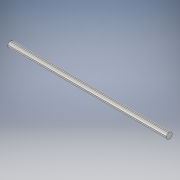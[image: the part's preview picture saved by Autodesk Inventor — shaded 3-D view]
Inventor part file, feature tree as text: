
AUTODESK INVENTOR PART (.ipt)
format: ipt  version: 2018 (Build 220112000, 112)  size: 107,008 bytes
history: native  units: in
note: dims shown in document units (in); Inventor stores cm internally (conversion verified against a paired STEP export)
features: extrude x1, fillet x1, plane x1, sketch x1
ambient origin geometry x8: Origin, YZ Plane, XZ Plane, XY Plane, X Axis, Y Axis, Z Axis, Center Point
bodies: Solid1 (feature_tree)
feature tree (4):
  extrude  "Extrusion1"  Depth=0.1181in
  fillet  "Fillet1"  Radius=3.3465in
  plane  "Work Plane1"
  sketch  "Sketch1"  dims[d0=0.1181in d1=0.1181in d2=3.3465in d3=0.0in d4=0.045in]
